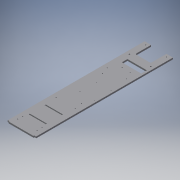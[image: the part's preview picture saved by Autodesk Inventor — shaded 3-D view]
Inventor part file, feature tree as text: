
AUTODESK INVENTOR PART (.ipt)
format: ipt  version: 2016 (Build 200138000, 138)  size: 377,344 bytes
history: native  units: in
note: dims shown in document units (in); Inventor stores cm internally (conversion verified against a paired STEP export)
features: extrude x21, sketch x21, fillet x1
ambient origin geometry x8: Origin, YZ Plane, XZ Plane, XY Plane, X Axis, Y Axis, Z Axis, Center Point
bodies: Solid1 (feature_tree)
feature tree (43):
  extrude  "Extrusion1"  Depth=3.94in
  extrude  "Extrusion3"  Depth=0.213in
  extrude  "Extrusion4"  Depth=2.9in
  extrude  "Extrusion5"  Depth=1.0in TaperAngle=0.0deg
  extrude  "Extrusion6"  Depth=0.25in
  extrude  "Extrusion7"  Depth=0.25in TaperAngle=0.0deg
  extrude  "Extrusion8"  Depth=0.1181in
  extrude  "Extrusion9"  Depth=2.147in TaperAngle=0.0deg
  extrude  "Extrusion10"  Depth=3.0in
  extrude  "Extrusion11"  Depth=0.477in
  extrude  "Extrusion12"  Depth=0.935in
  extrude  "Extrusion13"  Depth=0.3in
  extrude  "Extrusion14"  Depth=1.0in
  sketch  "Sketch17"  dims[d36=2.7in d37=0.7in]
  sketch  "Sketch18"  dims[d38=0.7in d39=2.7in]
  extrude  "Extrusion15"  Depth=0.7in
  extrude  "Extrusion16"  Depth=2.7in
  extrude  "Extrusion17"  Depth=0.1181in
  extrude  "Extrusion18"  Depth=0.1181in
  extrude  "Extrusion19"  Depth=0.15in
  extrude  "Extrusion20"  Depth=0.3in
  extrude  "Extrusion21"  Depth=0.3in
  extrude  "Extrusion22"  Depth=0.125in
  fillet  "Fillet1"  Radius=1.0in
  sketch  "Sketch1"  dims[d0=3.94in d1=14.0in]
  sketch  "Sketch5"  dims[d2=0.213in d3=0.0in d8=0.1181in]
  sketch  "Sketch6"  dims[d9=0.1181in d10=2.9in]
  sketch  "Sketch7"  dims[d11=0.379in d12=1.0in d13=0.0in]
  sketch  "Sketch8"  dims[d14=0.11in d15=0.25in]
  sketch  "Sketch9"  dims[d16=0.25in d17=1.0in d18=0.0in]
  sketch  "Sketch10"  dims[d19=0.1181in d20=0.1181in]
  sketch  "Sketch11"  dims[d21=10.0in d22=0.0in d23=2.147in d24=0.0in]
  sketch  "Sketch12"  dims[d25=2.147in d26=0.0in d27=3.0in]
  sketch  "Sketch13"  dims[d28=1.0in d29=0.477in]
  sketch  "Sketch14"  dims[d30=0.463in d31=0.935in]
  sketch  "Sketch15"  dims[d32=0.3in d33=0.3in]
  sketch  "Sketch16"  dims[d34=1.0in d35=1.0in]
  sketch  "Sketch19"  dims[d40=0.1181in d41=0.1181in]
  sketch  "Sketch20"  dims[d42=0.1181in d43=0.1181in]
  sketch  "Sketch21"  dims[d44=0.15in d45=1.0in]
  sketch  "Sketch22"  dims[d46=1.0in d47=0.3in]
  sketch  "Sketch23"  dims[d48=0.3in d49=0.3in]
  sketch  "Sketch24"  dims[d50=0.3in d51=3.0in d52=1.0in d53=1.0in d54=0.7in d55=2.147in d56=0.0in d57=5.579in d58=0.323in d59=0.086in d60=0.086in d62=2.036in d63=2.281in d64=2.281in d65=2.147in d66=0.0in d67=0.121in d68=0.341in d69=8.925in d75=1.0in d76=0.0in d89=0.599in d90=0.104in d91=2.958in d92=2.103in d93=0.08in d94=0.116in d95=1.472in d96=0.55in d97=2.958in d98=0.121in d99=0.104in d100=0.121in d101=0.104in d102=1.098in d103=0.297in d104=2.3788in d105=1.0in d106=0.0in d107=3.3244in d108=0.429in d109=0.5in d110=0.084in d111=0.084in d114=0.274in d115=1.0in d116=0.0in d117=0.1181in d119=4.148in d120=0.85in d121=0.1181in d122=0.941in d123=9.225in d124=1.0in d125=0.0in d128=7.3543in d129=2.887in d130=0.1181in d131=0.1181in d132=0.1181in d133=0.1181in d134=0.1181in d135=0.1181in d136=0.1181in d137=0.1181in d138=0.1181in d139=0.1181in d140=0.1181in d141=0.1181in d142=1.0in d143=0.0in d144=3.0in d145=0.0in d146=3.0in d147=0.0in d148=0.1181in d149=0.1181in d150=0.1181in d151=0.1181in d152=0.7in d153=0.7in d154=2.7in d155=2.7in d156=2.7in d157=1.0in d158=0.0in d159=0.213in d160=0.0in d161=0.1181in d162=0.1181in d163=1.098in d164=1.098in d165=0.213in d166=0.0in d167=0.213in d168=0.0in d169=0.15in d170=0.15in d171=0.213in d172=0.0in d173=0.899in d174=0.899in d175=0.213in d176=0.0in d177=0.125in]
